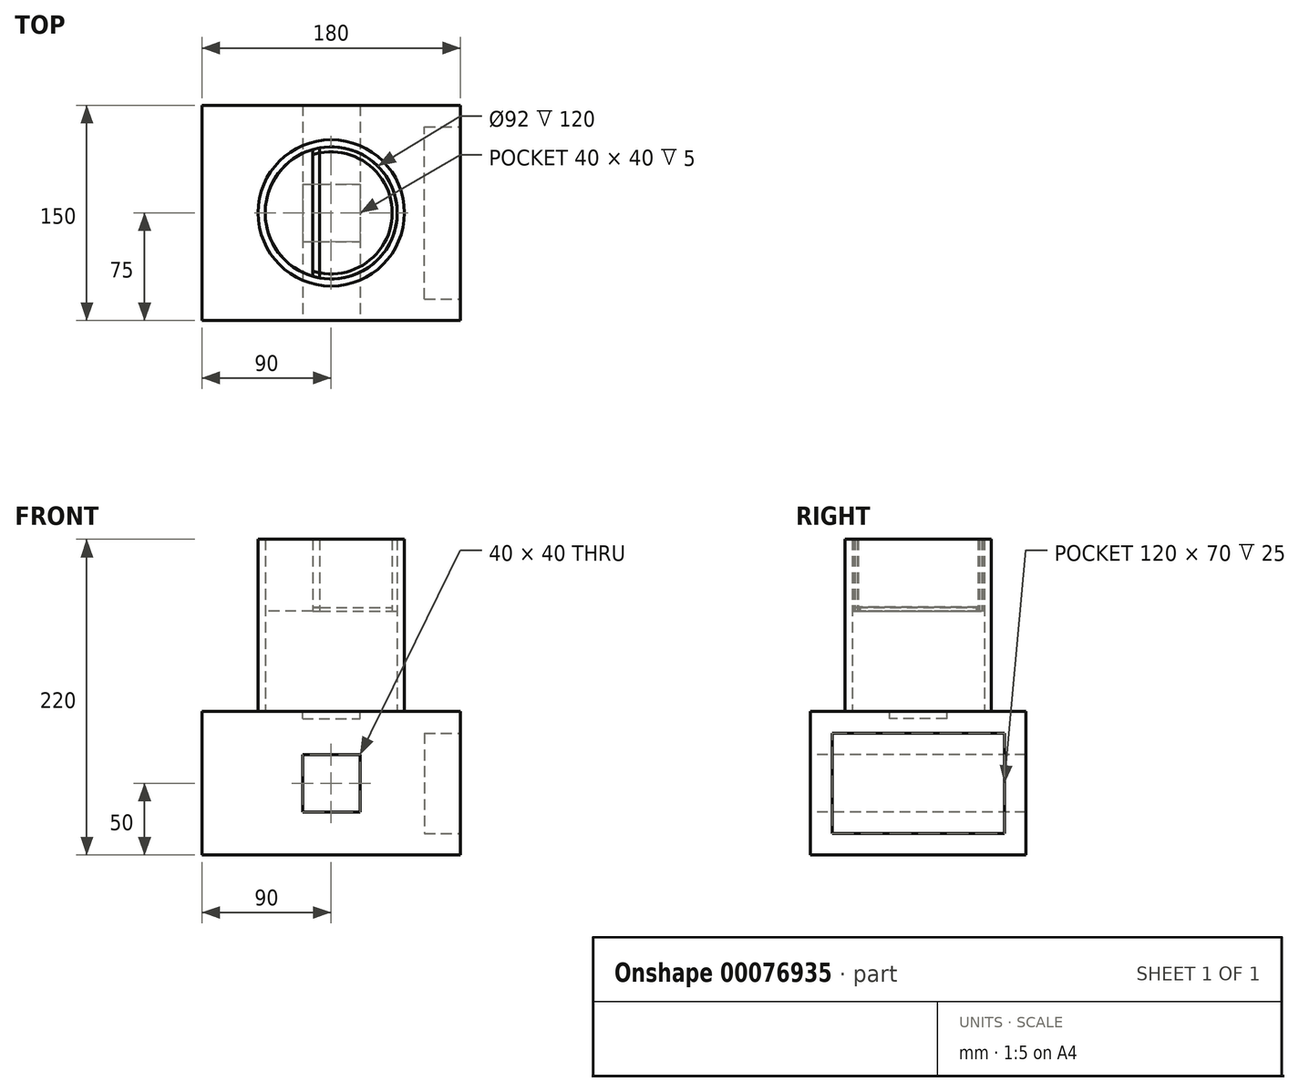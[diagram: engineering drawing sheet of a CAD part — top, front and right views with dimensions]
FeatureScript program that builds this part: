
annotation { "Feature Type Name" : "Feature", "Feature Type Description" : "" }
export const myFeature = defineFeature(function(context is Context, id is Id, definition is map)
    precondition{}
    {
        {
            var Q0;
            Q0=qCreatedBy(makeId("Top.planeOp"),FACE);
            var sketch = newSketch(context, id + "F0", { "sketchPlane" : qUnion([Q0])});
            skCircle(sketch, "E0", {"center": v(0, 0) * mm, "radius": 46 * mm});
            skCircle(sketch, "E1", {"center": v(0, 0) * mm, "radius": 51 * mm});
            skLineSegment(sketch, "E2.bottom", {"start": v(-20, 20) * mm, "end": v(20, 20) * mm});
            skLineSegment(sketch, "E2.top", {"start": v(-20, -20) * mm, "end": v(20, -20) * mm});
            skLineSegment(sketch, "E2.left", {"start": v(-20, 20) * mm, "end": v(-20, -20) * mm});
            skLineSegment(sketch, "E2.right", {"start": v(20, 20) * mm, "end": v(20, -20) * mm});
            skSolve(sketch);
        }
        {
            var Q0;
            Q0=makeQuery(id+"F0.imprint","IMPRINT",FACE,{"disambiguationData":[TD([[makeQuery(id+"F0.imprint","IMPRINT",EDGE,{"derivedFrom":sQuery(id+"F0.wireOp",EDGE,"E0")}),-1.0]])]});
            extrude(context, id + "F1", {"entities" : qUnion([Q0]), "depth" : 120 * mm});
        }
        {
            var Q0;
            Q0=qCreatedBy(makeId("Top.planeOp"),FACE);
            var sketch = newSketch(context, id + "F2", { "sketchPlane" : qUnion([Q0])});
            skLineSegment(sketch, "E3.bottom", {"start": v(-90, 75) * mm, "end": v(90, 75) * mm});
            skLineSegment(sketch, "E3.top", {"start": v(-90, -75) * mm, "end": v(90, -75) * mm});
            skLineSegment(sketch, "E3.left", {"start": v(-90, 75) * mm, "end": v(-90, -75) * mm});
            skLineSegment(sketch, "E3.right", {"start": v(90, 75) * mm, "end": v(90, -75) * mm});
            skSolve(sketch);
        }
        {
            var Q0;
            Q0=makeQuery(id+"F2.imprint","IMPRINT",FACE,{"disambiguationData":[TD([[makeQuery(id+"F2.imprint","IMPRINT",EDGE,{"derivedFrom":sQuery(id+"F2.wireOp",EDGE,"E3.bottom")}),-1.0]])]});
            extrude(context, id + "F3", {"entities" : qUnion([Q0]), "oppositeDirection" : true, "depth" : 100 * mm});
        }
        {
            var Q0;
            Q0=makeQuery(id+"F0.imprint","IMPRINT",FACE,{"disambiguationData":[TD([[makeQuery(id+"F0.imprint","IMPRINT",EDGE,{"derivedFrom":sQuery(id+"F0.wireOp",EDGE,"E2.bottom")}),-1.0]])]});
            extrude(context, id + "F4", {"entities" : qUnion([Q0]), "operationType" : NewBodyOperationType.REMOVE, "oppositeDirection" : true, "depth" : 5 * mm});
        }
        {
            var Q0;
            Q0=makeQuery(id+"F3.opExtrude","SWEPT_FACE",FACE,{"disambiguationData":[OSD([sQuery(id+"F2.wireOp",EDGE,"E3.top")])]});
            cPlane(context, id + "F5", {"entities" : qUnion([Q0]), "cplaneType" : CPlaneType.OFFSET, "offset" : 0 * mm, "width" : 150 * mm, "height" : 150 * mm});
        }
        {
            var Q0;
            Q0=qCreatedBy(id+"F5.planeOp",FACE);
            var sketch = newSketch(context, id + "F6", { "sketchPlane" : qUnion([Q0])});
            skLineSegment(sketch, "E4.bottom", {"start": v(-20, -30) * mm, "end": v(20, -30) * mm});
            skLineSegment(sketch, "E4.top", {"start": v(-20, -70) * mm, "end": v(20, -70) * mm});
            skLineSegment(sketch, "E4.left", {"start": v(-20, -30) * mm, "end": v(-20, -70) * mm});
            skLineSegment(sketch, "E4.right", {"start": v(20, -30) * mm, "end": v(20, -70) * mm});
            skSolve(sketch);
        }
        {
            var Q0;
            Q0=makeQuery(id+"F6.imprint","IMPRINT",FACE,{"disambiguationData":[TD([[makeQuery(id+"F6.imprint","IMPRINT",EDGE,{"derivedFrom":sQuery(id+"F6.wireOp",EDGE,"E4.bottom")}),-1.0]])]});
            extrude(context, id + "F7", {"entities" : qUnion([Q0]), "operationType" : NewBodyOperationType.REMOVE, "endBound" : BoundingType.THROUGH_ALL, "oppositeDirection" : true, "depth" : 25 * mm});
        }
        {
            var Q0;
            Q0=makeQuery(id+"F3.opExtrude","SWEPT_FACE",FACE,{"disambiguationData":[OSD([sQuery(id+"F2.wireOp",EDGE,"E3.right")])]});
            cPlane(context, id + "F8", {"entities" : qUnion([Q0]), "cplaneType" : CPlaneType.OFFSET, "offset" : 0 * mm, "width" : 150 * mm, "height" : 150 * mm});
        }
        {
            var Q0;
            Q0=qCreatedBy(id+"F8.planeOp",FACE);
            var sketch = newSketch(context, id + "F9", { "sketchPlane" : qUnion([Q0])});
            skLineSegment(sketch, "E5.bottom", {"start": v(-60, -15) * mm, "end": v(60, -15) * mm});
            skLineSegment(sketch, "E5.top", {"start": v(-60, -85) * mm, "end": v(60, -85) * mm});
            skLineSegment(sketch, "E5.left", {"start": v(-60, -15) * mm, "end": v(-60, -85) * mm});
            skLineSegment(sketch, "E5.right", {"start": v(60, -15) * mm, "end": v(60, -85) * mm});
            skSolve(sketch);
        }
        {
            var Q0;
            Q0=makeQuery(id+"F9.imprint","IMPRINT",FACE,{"disambiguationData":[TD([[makeQuery(id+"F9.imprint","IMPRINT",EDGE,{"derivedFrom":sQuery(id+"F9.wireOp",EDGE,"E5.bottom")}),-1.0]])]});
            extrude(context, id + "F10", {"entities" : qUnion([Q0]), "operationType" : NewBodyOperationType.REMOVE, "oppositeDirection" : true, "depth" : 25 * mm});
        }
        {
            var Q0;
            Q0=makeQuery(id+"F3.opExtrude","CAP_FACE",FACE,{"disambiguationData":[OSD([sQuery(id+"F2.wireOp",EDGE,"E3.bottom"),sQuery(id+"F2.wireOp",EDGE,"E3.top"),sQuery(id+"F2.wireOp",EDGE,"E3.left"),sQuery(id+"F2.wireOp",EDGE,"E3.right")])],"isStart":true});
            cPlane(context, id + "F11", {"entities" : qUnion([Q0]), "cplaneType" : CPlaneType.OFFSET, "offset" : 70 * mm, "width" : 150 * mm, "height" : 150 * mm});
        }
        {
            var Q0;
            Q0=qCreatedBy(id+"F11.planeOp",FACE);
            var sketch = newSketch(context, id + "F12", { "sketchPlane" : qUnion([Q0])});
            skCircle(sketch, "E6", {"center": v(0, 0) * mm, "radius": 42.5 * mm});
            skLineSegment(sketch, "E7", {"start": v(-8, 45.46) * mm, "end": v(-8, -45.8) * mm});
            skLineSegment(sketch, "E8", {"start": v(-13, -44.75) * mm, "end": v(-13, 44.42) * mm});
            skCircle(sketch, "E9", {"center": v(0, 0) * mm, "radius": 46 * mm});
            skSolve(sketch);
        }
        {
            var Q0;
            {var subQ0=sQuery(id+"F12.wireOp",EDGE,"E7");var subQ1=sQuery(id+"F12.wireOp",EDGE,"E6");var subQ2=makeQuery(id+"F12.imprint","INTERSECT",VERTEX,{"disambiguationData":[OD(0.0)],"derivedFrom":[subQ1,subQ0]});Q0=makeQuery(id+"F12.imprint","IMPRINT",FACE,{"disambiguationData":[TD([[makeQuery(id+"F12.imprint","IMPRINT",EDGE,{"disambiguationData":[TD([[subQ2,1.0]])],"derivedFrom":subQ1}),1.0]])]});}
            extrude(context, id + "F13", {"entities" : qUnion([Q0]), "depth" : 2.5 * mm});
        }
        {
            var Q0;
            {var subQ0=sQuery(id+"F12.wireOp",EDGE,"E7");var subQ1=sQuery(id+"F12.wireOp",EDGE,"E6");var subQ2=makeQuery(id+"F12.imprint","INTERSECT",VERTEX,{"disambiguationData":[OD(0.0)],"derivedFrom":[subQ1,subQ0]});Q0=makeQuery(id+"F12.imprint","IMPRINT",FACE,{"disambiguationData":[TD([[makeQuery(id+"F12.imprint","IMPRINT",EDGE,{"disambiguationData":[TD([[subQ2,1.0]])],"derivedFrom":subQ1}),-1.0]])]});}
            var Q1;
            {var subQ0=sQuery(id+"F12.wireOp",EDGE,"E8");var subQ1=sQuery(id+"F12.wireOp",EDGE,"E6");var subQ2=makeQuery(id+"F12.imprint","INTERSECT",VERTEX,{"disambiguationData":[OD(0.0)],"derivedFrom":[subQ1,subQ0]});Q1=makeQuery(id+"F12.imprint","IMPRINT",FACE,{"disambiguationData":[TD([[makeQuery(id+"F12.imprint","IMPRINT",EDGE,{"disambiguationData":[TD([[subQ2,1.0]])],"derivedFrom":subQ1}),-1.0]])]});}
            var Q2;
            {var subQ0=sQuery(id+"F12.wireOp",EDGE,"E8");var subQ1=sQuery(id+"F12.wireOp",EDGE,"E6");var subQ2=makeQuery(id+"F12.imprint","INTERSECT",VERTEX,{"disambiguationData":[OD(1.0)],"derivedFrom":[subQ1,subQ0]});Q2=makeQuery(id+"F12.imprint","IMPRINT",FACE,{"disambiguationData":[TD([[makeQuery(id+"F12.imprint","IMPRINT",EDGE,{"disambiguationData":[TD([[subQ2,-1.0]])],"derivedFrom":subQ1}),-1.0]])]});}
            var Q3;
            {var subQ0=sQuery(id+"F12.wireOp",EDGE,"E8");var subQ1=sQuery(id+"F12.wireOp",EDGE,"E6");var subQ2=makeQuery(id+"F12.imprint","INTERSECT",VERTEX,{"disambiguationData":[OD(0.0)],"derivedFrom":[subQ1,subQ0]});Q3=makeQuery(id+"F12.imprint","IMPRINT",FACE,{"disambiguationData":[TD([[makeQuery(id+"F12.imprint","IMPRINT",EDGE,{"disambiguationData":[TD([[subQ2,1.0]])],"derivedFrom":subQ1}),1.0]])]});}
            extrude(context, id + "F14", {"entities" : qUnion([Q0, Q1, Q2, Q3]), "depth" : 50 * mm});
        }
        {
            var Q0;
            {var subQ0=sQuery(id+"F12.wireOp",EDGE,"E8");var subQ1=sQuery(id+"F12.wireOp",EDGE,"E6");var subQ2=makeQuery(id+"F12.imprint","INTERSECT",VERTEX,{"disambiguationData":[OD(0.0)],"derivedFrom":[subQ1,subQ0]});Q0=makeQuery(id+"F12.imprint","IMPRINT",FACE,{"disambiguationData":[TD([[makeQuery(id+"F12.imprint","IMPRINT",EDGE,{"disambiguationData":[TD([[subQ2,-1.0]])],"derivedFrom":subQ1}),-1.0]])]});}
            extrude(context, id + "F15", {"entities" : qUnion([Q0]), "depth" : 2.5 * mm});
        }
        {
            var Q0;
            {var subQ0=sQuery(id+"F12.wireOp",EDGE,"E8");var subQ1=sQuery(id+"F12.wireOp",EDGE,"E6");var subQ2=makeQuery(id+"F12.imprint","INTERSECT",VERTEX,{"disambiguationData":[OD(0.0)],"derivedFrom":[subQ1,subQ0]});Q0=makeQuery(id+"F12.imprint","IMPRINT",FACE,{"disambiguationData":[TD([[makeQuery(id+"F12.imprint","IMPRINT",EDGE,{"disambiguationData":[TD([[subQ2,-1.0]])],"derivedFrom":subQ1}),1.0]])]});}
            extrude(context, id + "F16", {"entities" : qUnion([Q0]), "depth" : 3 * mm});
        }
    });
